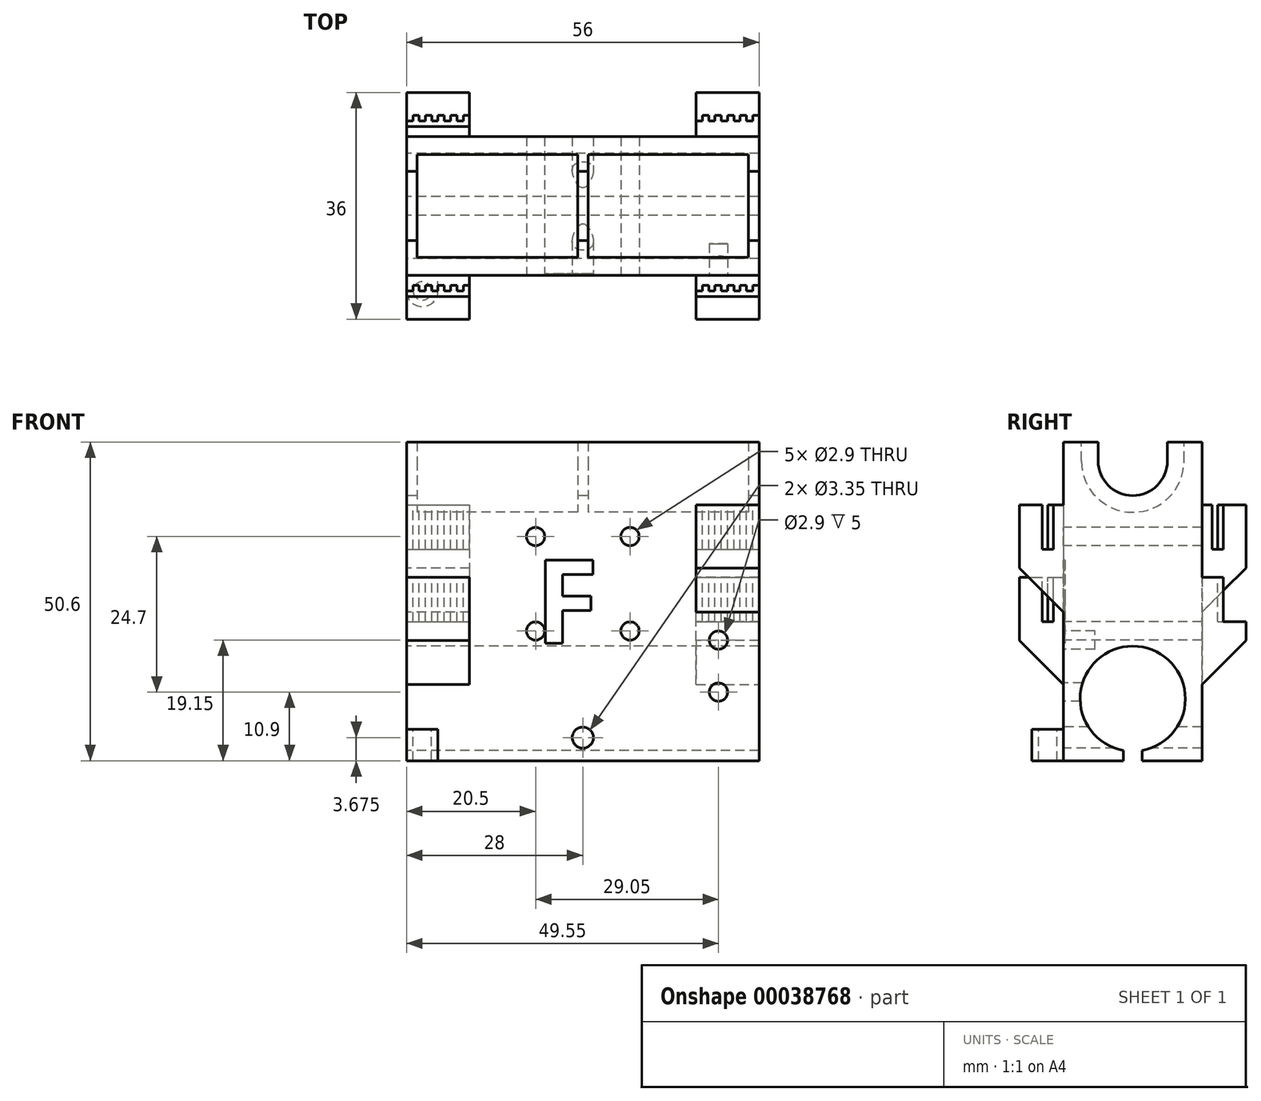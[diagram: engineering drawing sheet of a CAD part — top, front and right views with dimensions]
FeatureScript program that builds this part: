
annotation { "Feature Type Name" : "Feature", "Feature Type Description" : "" }
export const myFeature = defineFeature(function(context is Context, id is Id, definition is map)
    precondition{}
    {
        {
            assignVariable(context, id + "F0", {"name" : "LM8LUU", "anyValue" : 25.5});
        }
        {
            assignVariable(context, id + "F1", {"name" : "length", "anyValue" : 56});
        }
        {
            assignVariable(context, id + "F2", {"name" : "height", "anyValue" : 50.6});
        }
        {
            assignVariable(context, id + "F3", {"name" : "divider", "anyValue" : (getVariable(context, 'length') - 2 * getVariable(context, 'LM8LUU')) / 3});
        }
        {
            var Q0;
            Q0=qCreatedBy(makeId("Top.planeOp"),FACE);
            var sketch = newSketch(context, id + "F4", { "sketchPlane" : qUnion([Q0])});
            skLineSegment(sketch, "E0.bottom", {"start": v(0, 0) * mm, "end": v(56, 0) * mm});
            skLineSegment(sketch, "E0.top", {"start": v(0, 22) * mm, "end": v(56, 22) * mm});
            skLineSegment(sketch, "E0.left", {"start": v(0, 0) * mm, "end": v(0, 22) * mm});
            skLineSegment(sketch, "E0.right", {"start": v(56, 0) * mm, "end": v(56, 22) * mm});
            skSolve(sketch);
        }
        {
            var Q0;
            Q0=qSketchRegion(id+"F4",true);
            extrude(context, id + "F5", {"entities" : qUnion([Q0]), "depth" : (getVariable(context, 'height')) * mm});
        }
        {
            var Q0;
            Q0=makeQuery(id+"F5.opExtrude","SWEPT_FACE",FACE,{"disambiguationData":[OSD([sQuery(id+"F4.wireOp",EDGE,"E0.left")])]});
            var sketch = newSketch(context, id + "F6", { "sketchPlane" : qUnion([Q0])});
            skCircle(sketch, "E1", {"center": v(-11, 9.85) * mm, "radius": 8.35 * mm});
            skCircle(sketch, "E2", {"center": v(-11, 47.6) * mm, "radius": 5.5 * mm});
            skLineSegment(sketch, "E3", {"start": v(-22, 47.6) * mm, "end": v(0, 47.6) * mm, "construction": true});
            skLineSegment(sketch, "E4", {"start": v(-16.5, 50.6) * mm, "end": v(-16.5, 47.6) * mm});
            skLineSegment(sketch, "E5", {"start": v(-5.5, 50.6) * mm, "end": v(-5.5, 47.6) * mm});
            skLineSegment(sketch, "E6", {"start": v(-22, 9.85) * mm, "end": v(0, 9.85) * mm, "construction": true});
            skLineSegment(sketch, "E7", {"start": v(-11, 9.85) * mm, "end": v(-11, 0) * mm, "construction": true});
            skLineSegment(sketch, "E8", {"start": v(-11, 0) * mm, "end": v(-12.5, 0) * mm});
            skLineSegment(sketch, "E9", {"start": v(-12.5, 0) * mm, "end": v(-12.5, 1.64) * mm});
            skLineSegment(sketch, "E10", {"start": v(-12.5, 1.64) * mm, "end": v(-9.5, 1.64) * mm});
            skLineSegment(sketch, "E11", {"start": v(-9.5, 1.64) * mm, "end": v(-9.5, 0) * mm});
            skLineSegment(sketch, "E12", {"start": v(-9.5, 0) * mm, "end": v(-11, 0) * mm});
            skLineSegment(sketch, "E13", {"start": v(-11, 15.6) * mm, "end": v(-11, 18.2) * mm});
            skLineSegment(sketch, "E14", {"start": v(-11, 15.6) * mm, "end": v(-6.05, 16.58) * mm});
            skLineSegment(sketch, "E15", {"start": v(-11, 15.6) * mm, "end": v(-15.95, 16.58) * mm});
            skCircle(sketch, "E16", {"center": v(-11, 47.6) * mm, "radius": 8.15 * mm});
            skLineSegment(sketch, "E17", {"start": v(-2.85, 47.6) * mm, "end": v(-2.85, 50.6) * mm});
            skLineSegment(sketch, "E18", {"start": v(-19.15, 47.6) * mm, "end": v(-19.15, 50.6) * mm});
            skSolve(sketch);
        }
        {
            var Q0;
            {var subQ0=sQuery(id+"F6.wireOp",EDGE,"E14");var subQ1=sQuery(id+"F6.wireOp",EDGE,"E1");var subQ3=makeQuery(id+"F6.imprint","INTERSECT",VERTEX,{"disambiguationData":[OD(0.0)],"derivedFrom":[subQ1,subQ0]});Q0=makeQuery(id+"F6.imprint","IMPRINT",FACE,{"disambiguationData":[TD([[makeQuery(id+"F6.imprint","IMPRINT",EDGE,{"disambiguationData":[TD([[subQ3,-1.0]])],"derivedFrom":subQ1}),1.0]])]});}
            var Q1;
            {var subQ0=sQuery(id+"F6.wireOp",EDGE,"E15");var subQ1=sQuery(id+"F6.wireOp",EDGE,"E1");var subQ3=makeQuery(id+"F6.imprint","INTERSECT",VERTEX,{"disambiguationData":[OD(0.0)],"derivedFrom":[subQ1,subQ0]});Q1=makeQuery(id+"F6.imprint","IMPRINT",FACE,{"disambiguationData":[TD([[makeQuery(id+"F6.imprint","IMPRINT",EDGE,{"disambiguationData":[TD([[subQ3,1.0]])],"derivedFrom":subQ1}),1.0]])]});}
            var Q2;
            Q2=makeQuery(id+"F6.imprint","IMPRINT",FACE,{"disambiguationData":[TD([[makeQuery(id+"F6.imprint","IMPRINT",EDGE,{"derivedFrom":sQuery(id+"F6.wireOp",EDGE,"E8")}),-1.0]])]});
            var Q3;
            {var subQ0=sQuery(id+"F6.wireOp",EDGE,"E10");Q3=makeQuery(id+"F6.imprint","IMPRINT",FACE,{"disambiguationData":[TD([[makeQuery(id+"F6.imprint","IMPRINT",EDGE,{"derivedFrom":subQ0}),-1.0]])]});}
            var Q4;
            {var subQ3=sQuery(id+"F6.wireOp",EDGE,"E13");Q4=makeQuery(id+"F6.imprint","IMPRINT",FACE,{"disambiguationData":[TD([[makeQuery(id+"F6.imprint","IMPRINT",EDGE,{"derivedFrom":subQ3}),-1.0]])]});}
            var Q5;
            {var subQ3=sQuery(id+"F6.wireOp",EDGE,"E13");Q5=makeQuery(id+"F6.imprint","IMPRINT",FACE,{"disambiguationData":[TD([[makeQuery(id+"F6.imprint","IMPRINT",EDGE,{"derivedFrom":subQ3}),1.0]])]});}
            var Q6;
            {var subQ7=sQuery(id+"F6.wireOp",EDGE,"E10");Q6=makeQuery(id+"F6.imprint","IMPRINT",FACE,{"disambiguationData":[TD([[makeQuery(id+"F6.imprint","IMPRINT",EDGE,{"derivedFrom":subQ7}),1.0]])]});}
            var Q7;
            {var subQ3=sQuery(id+"F6.wireOp",EDGE,"E5");Q7=makeQuery(id+"F6.imprint","IMPRINT",FACE,{"disambiguationData":[TD([[makeQuery(id+"F6.imprint","IMPRINT",EDGE,{"derivedFrom":subQ3}),-1.0]])]});}
            var Q8;
            {var subQ0=sQuery(id+"F6.wireOp",EDGE,"E4");Q8=makeQuery(id+"F6.imprint","IMPRINT",FACE,{"disambiguationData":[TD([[makeQuery(id+"F6.imprint","IMPRINT",EDGE,{"derivedFrom":subQ0}),1.0]])]});}
            var Q9;
            {var subQ0=sQuery(id+"F6.wireOp",EDGE,"E4");Q9=makeQuery(id+"F6.imprint","IMPRINT",FACE,{"disambiguationData":[TD([[makeQuery(id+"F6.imprint","IMPRINT",EDGE,{"derivedFrom":subQ0}),1.0]])]});}
            var Q10;
            {var subQ3=sQuery(id+"F6.wireOp",EDGE,"E5");Q10=makeQuery(id+"F6.imprint","IMPRINT",FACE,{"disambiguationData":[TD([[makeQuery(id+"F6.imprint","IMPRINT",EDGE,{"derivedFrom":subQ3}),-1.0]])]});}
            var Q11;
            {var subQ1=sQuery(id+"F6.wireOp",EDGE,"E2");var subQ4=makeQuery(id+"F6.imprint","INTERSECT",VERTEX,{"derivedFrom":[subQ1,sQuery(id+"F6.wireOp",EDGE,"E5")]});Q11=makeQuery(id+"F6.imprint","IMPRINT",FACE,{"disambiguationData":[TD([[makeQuery(id+"F6.imprint","IMPRINT",EDGE,{"disambiguationData":[TD([[subQ4,-1.0]])],"derivedFrom":subQ1}),1.0]])]});}
            extrude(context, id + "F7", {"entities" : qUnion([Q0, Q1, Q2, Q3, Q4, Q5, Q6, Q7, Q8, Q9, Q10, Q11]), "operationType" : NewBodyOperationType.REMOVE, "endBound" : BoundingType.THROUGH_ALL, "oppositeDirection" : true, "depth" : 25 * mm});
        }
        {
            var Q0;
            {var subQ6=sQuery(id+"F6.wireOp",EDGE,"E4");Q0=makeQuery(id+"F6.imprint","IMPRINT",FACE,{"disambiguationData":[TD([[makeQuery(id+"F6.imprint","IMPRINT",EDGE,{"derivedFrom":subQ6}),-1.0]])]});}
            var Q1;
            {var subQ0=sQuery(id+"F6.wireOp",EDGE,"E18");Q1=makeQuery(id+"F6.imprint","IMPRINT",FACE,{"disambiguationData":[TD([[makeQuery(id+"F6.imprint","IMPRINT",EDGE,{"derivedFrom":subQ0}),-1.0]])]});}
            var Q2;
            {var subQ0=sQuery(id+"F6.wireOp",EDGE,"E17");Q2=makeQuery(id+"F6.imprint","IMPRINT",FACE,{"disambiguationData":[TD([[makeQuery(id+"F6.imprint","IMPRINT",EDGE,{"derivedFrom":subQ0}),1.0]])]});}
            extrude(context, id + "F8", {"entities" : qUnion([Q0, Q1, Q2]), "operationType" : NewBodyOperationType.REMOVE, "oppositeDirection" : true, "depth" : (getVariable(context, 'divider') + (getVariable(context, 'LM8LUU'))) * mm, "hasSecondDirection" : true, "secondDirectionOppositeDirection" : true, "secondDirectionDepth" : (getVariable(context, 'divider')) * mm});
        }
        {
            var Q0;
            Q0=makeQuery(id+"F8.boolean.opBoolean","COPY",FACE,{"derivedFrom":makeQuery(id+"F8.opExtrude","CAP_FACE",FACE,{"disambiguationData":[OSD([sQuery(id+"F4.wireOp",EDGE,"E0.left"),sQuery(id+"F6.wireOp",EDGE,"E2"),sQuery(id+"F6.wireOp",EDGE,"E4"),sQuery(id+"F6.wireOp",EDGE,"E5"),sQuery(id+"F6.wireOp",EDGE,"E16"),sQuery(id+"F6.wireOp",EDGE,"E17"),sQuery(id+"F6.wireOp",EDGE,"E18")])],"isStart":false})});
            extrude(context, id + "F9", {"entities" : qUnion([Q0]), "operationType" : NewBodyOperationType.REMOVE, "oppositeDirection" : true, "depth" : (getVariable(context, 'divider') + getVariable(context, 'LM8LUU')) * mm, "hasSecondDirection" : true, "secondDirectionOppositeDirection" : true, "secondDirectionDepth" : (getVariable(context, 'divider')) * mm});
        }
        {
            var Q0;
            Q0=makeQuery(id+"F5.opExtrude","SWEPT_FACE",FACE,{"disambiguationData":[OSD([sQuery(id+"F4.wireOp",EDGE,"E0.bottom")])]});
            var sketch = newSketch(context, id + "F10", { "sketchPlane" : qUnion([Q0])});
            skLineSegment(sketch, "E19.bottom", {"start": v(0, 29.1) * mm, "end": v(10, 29.1) * mm});
            skLineSegment(sketch, "E19.top", {"start": v(0, 9.1) * mm, "end": v(10, 9.1) * mm});
            skLineSegment(sketch, "E19.left", {"start": v(0, 29.1) * mm, "end": v(0, 9.1) * mm});
            skLineSegment(sketch, "E19.right", {"start": v(10, 29.1) * mm, "end": v(10, 9.1) * mm});
            skLineSegment(sketch, "E20.bottom", {"start": v(56, 40.6) * mm, "end": v(46, 40.6) * mm});
            skLineSegment(sketch, "E20.top", {"start": v(56, 20.6) * mm, "end": v(46, 20.6) * mm});
            skLineSegment(sketch, "E20.left", {"start": v(56, 40.6) * mm, "end": v(56, 20.6) * mm});
            skLineSegment(sketch, "E20.right", {"start": v(46, 40.6) * mm, "end": v(46, 20.6) * mm});
            skPoint(sketch, "E21", {"position": v(0, 47.6) * mm});
            skPoint(sketch, "E22", {"position": v(0, 8.6) * mm});
            skSolve(sketch);
        }
        {
            var Q0;
            Q0=qSketchRegion(id+"F10",true);
            extrude(context, id + "F11", {"entities" : qUnion([Q0]), "operationType" : NewBodyOperationType.ADD, "depth" : 7 * mm});
        }
        {
            var Q0;
            Q0=makeQuery(id+"F11.opExtrude","CAP_EDGE",EDGE,{"disambiguationData":[OSD([sQuery(id+"F10.wireOp",EDGE,"E19.top")])],"isStart":false});
            var Q1;
            Q1=makeQuery(id+"F11.opExtrude","CAP_EDGE",EDGE,{"disambiguationData":[OSD([sQuery(id+"F10.wireOp",EDGE,"E20.top")])],"isStart":false});
            chamfer(context, id + "F12", {"entities" : qUnion([Q0, Q1]), "width" : 10 * mm, "tangentPropagation" : true});
        }
        {
            var Q0;
            Q0=makeQuery(id+"F11.opExtrude","SWEPT_FACE",FACE,{"disambiguationData":[OSD([sQuery(id+"F10.wireOp",EDGE,"E19.bottom")])]});
            var sketch = newSketch(context, id + "F13", { "sketchPlane" : qUnion([Q0])});
            skLineSegment(sketch, "E23", {"start": v(-935.9, 0) * mm, "end": v(-935.88, -4.54) * mm});
            skLineSegment(sketch, "E24.left", {"start": v(0, -3.4) * mm, "end": v(0, -1.6) * mm});
            skLineSegment(sketch, "E25", {"start": v(6, -2.5) * mm, "end": v(7, -2.5) * mm});
            skLineSegment(sketch, "E26", {"start": v(4, -2.5) * mm, "end": v(5, -2.5) * mm});
            skLineSegment(sketch, "E27", {"start": v(0, -2.5) * mm, "end": v(1, -2.5) * mm});
            skLineSegment(sketch, "E28", {"start": v(7, -1.6) * mm, "end": v(8, -1.6) * mm});
            skLineSegment(sketch, "E29", {"start": v(2, -2.5) * mm, "end": v(3, -2.5) * mm});
            skLineSegment(sketch, "E30", {"start": v(3, -1.6) * mm, "end": v(4, -1.6) * mm});
            skLineSegment(sketch, "E31", {"start": v(8, -2.5) * mm, "end": v(9, -2.5) * mm});
            skLineSegment(sketch, "E32", {"start": v(8, -1.6) * mm, "end": v(8, -2.5) * mm});
            skLineSegment(sketch, "E33", {"start": v(9, -2.5) * mm, "end": v(9, -1.6) * mm});
            skLineSegment(sketch, "E34", {"start": v(10, -1.6) * mm, "end": v(10, -2.5) * mm});
            skLineSegment(sketch, "E35", {"start": v(6, -1.6) * mm, "end": v(6, -2.5) * mm});
            skLineSegment(sketch, "E36", {"start": v(2, -1.6) * mm, "end": v(2, -2.5) * mm});
            skLineSegment(sketch, "E37", {"start": v(1, -1.6) * mm, "end": v(2, -1.6) * mm});
            skLineSegment(sketch, "E38", {"start": v(1, -2.5) * mm, "end": v(1, -1.6) * mm});
            skLineSegment(sketch, "E39", {"start": v(9, -1.6) * mm, "end": v(10, -1.6) * mm});
            skLineSegment(sketch, "E40", {"start": v(5, -1.6) * mm, "end": v(6, -1.6) * mm});
            skLineSegment(sketch, "E41", {"start": v(5, -2.5) * mm, "end": v(5, -1.6) * mm});
            skLineSegment(sketch, "E42", {"start": v(3, -2.5) * mm, "end": v(3, -1.6) * mm});
            skLineSegment(sketch, "E43", {"start": v(4, -1.6) * mm, "end": v(4, -2.5) * mm});
            skLineSegment(sketch, "E44", {"start": v(7, -2.5) * mm, "end": v(7, -1.6) * mm});
            skLineSegment(sketch, "E45", {"start": v(0, -1.6) * mm, "end": v(0, -2.5) * mm});
            skLineSegment(sketch, "E46", {"start": v(10, -2.5) * mm, "end": v(10, -3.4) * mm});
            skLineSegment(sketch, "E47", {"start": v(0, -3.4) * mm, "end": v(10, -3.4) * mm});
            skLineSegment(sketch, "E48", {"start": v(5.3, -1.6) * mm, "end": v(5.3, 0) * mm});
            skSolve(sketch);
        }
        {
            var Q0;
            Q0=qSketchRegion(id+"F13",true);
            extrude(context, id + "F14", {"entities" : qUnion([Q0]), "operationType" : NewBodyOperationType.REMOVE, "oppositeDirection" : true, "depth" : 7 * mm});
        }
        {
            var Q0;
            Q0=makeQuery(id+"F11.opExtrude","SWEPT_FACE",FACE,{"disambiguationData":[OSD([sQuery(id+"F10.wireOp",EDGE,"E20.bottom")])]});
            var sketch = newSketch(context, id + "F15", { "sketchPlane" : qUnion([Q0])});
            skLineSegment(sketch, "E49.left", {"start": v(46, -3.4) * mm, "end": v(46, -1.6) * mm});
            skLineSegment(sketch, "E50", {"start": v(52, -2.5) * mm, "end": v(53, -2.5) * mm});
            skLineSegment(sketch, "E51", {"start": v(50, -2.5) * mm, "end": v(51, -2.5) * mm});
            skLineSegment(sketch, "E52", {"start": v(46, -2.5) * mm, "end": v(47, -2.5) * mm});
            skLineSegment(sketch, "E53", {"start": v(53, -1.6) * mm, "end": v(54, -1.6) * mm});
            skLineSegment(sketch, "E54", {"start": v(48, -2.5) * mm, "end": v(49, -2.5) * mm});
            skLineSegment(sketch, "E55", {"start": v(49, -1.6) * mm, "end": v(50, -1.6) * mm});
            skLineSegment(sketch, "E56", {"start": v(54, -2.5) * mm, "end": v(55, -2.5) * mm});
            skLineSegment(sketch, "E57", {"start": v(54, -1.6) * mm, "end": v(54, -2.5) * mm});
            skLineSegment(sketch, "E58", {"start": v(55, -2.5) * mm, "end": v(55, -1.6) * mm});
            skLineSegment(sketch, "E59", {"start": v(56, -1.6) * mm, "end": v(56, -2.5) * mm});
            skLineSegment(sketch, "E60", {"start": v(52, -1.6) * mm, "end": v(52, -2.5) * mm});
            skLineSegment(sketch, "E61", {"start": v(48, -1.6) * mm, "end": v(48, -2.5) * mm});
            skLineSegment(sketch, "E62", {"start": v(47, -1.6) * mm, "end": v(48, -1.6) * mm});
            skLineSegment(sketch, "E63", {"start": v(47, -2.5) * mm, "end": v(47, -1.6) * mm});
            skLineSegment(sketch, "E64", {"start": v(55, -1.6) * mm, "end": v(56, -1.6) * mm});
            skLineSegment(sketch, "E65", {"start": v(51, -1.6) * mm, "end": v(52, -1.6) * mm});
            skLineSegment(sketch, "E66", {"start": v(51, -2.5) * mm, "end": v(51, -1.6) * mm});
            skLineSegment(sketch, "E67", {"start": v(49, -2.5) * mm, "end": v(49, -1.6) * mm});
            skLineSegment(sketch, "E68", {"start": v(50, -1.6) * mm, "end": v(50, -2.5) * mm});
            skLineSegment(sketch, "E69", {"start": v(53, -2.5) * mm, "end": v(53, -1.6) * mm});
            skLineSegment(sketch, "E70", {"start": v(46, -1.6) * mm, "end": v(46, -2.5) * mm});
            skLineSegment(sketch, "E71", {"start": v(56, -2.5) * mm, "end": v(56, -3.4) * mm});
            skLineSegment(sketch, "E72", {"start": v(46, -3.4) * mm, "end": v(56, -3.4) * mm});
            skLineSegment(sketch, "E73", {"start": v(51.23, -1.6) * mm, "end": v(51.23, 0) * mm});
            skSolve(sketch);
        }
        {
            var Q0;
            Q0=qSketchRegion(id+"F15",true);
            extrude(context, id + "F16", {"entities" : qUnion([Q0]), "operationType" : NewBodyOperationType.REMOVE, "oppositeDirection" : true, "depth" : 7 * mm});
        }
        {
            var Q0;
            Q0=makeQuery(id+"F5.opExtrude","SWEPT_FACE",FACE,{"disambiguationData":[OSD([sQuery(id+"F4.wireOp",EDGE,"E0.top")])]});
            var sketch = newSketch(context, id + "F17", { "sketchPlane" : qUnion([Q0])});
            skLineSegment(sketch, "E74.bottom", {"start": v(-56, 9.1) * mm, "end": v(-46, 9.1) * mm});
            skLineSegment(sketch, "E74.top", {"start": v(-56, 29.1) * mm, "end": v(-46, 29.1) * mm});
            skLineSegment(sketch, "E74.left", {"start": v(-56, 9.1) * mm, "end": v(-56, 29.1) * mm});
            skLineSegment(sketch, "E74.right", {"start": v(-46, 9.1) * mm, "end": v(-46, 29.1) * mm});
            skLineSegment(sketch, "E75.bottom", {"start": v(0, 40.6) * mm, "end": v(-10, 40.6) * mm});
            skLineSegment(sketch, "E75.top", {"start": v(0, 20.6) * mm, "end": v(-10, 20.6) * mm});
            skLineSegment(sketch, "E75.left", {"start": v(0, 40.6) * mm, "end": v(0, 20.6) * mm});
            skLineSegment(sketch, "E75.right", {"start": v(-10, 40.6) * mm, "end": v(-10, 20.6) * mm});
            skSolve(sketch);
        }
        {
            var Q0;
            Q0=qSketchRegion(id+"F17",true);
            extrude(context, id + "F18", {"entities" : qUnion([Q0]), "operationType" : NewBodyOperationType.ADD, "depth" : 7 * mm});
        }
        {
            var Q0;
            Q0=makeQuery(id+"F18.opExtrude","SWEPT_FACE",FACE,{"disambiguationData":[OSD([sQuery(id+"F17.wireOp",EDGE,"E74.top")])]});
            var sketch = newSketch(context, id + "F19", { "sketchPlane" : qUnion([Q0])});
            skLineSegment(sketch, "E76.left", {"start": v(46, 23.6) * mm, "end": v(46, 25.4) * mm});
            skLineSegment(sketch, "E77", {"start": v(52, 24.5) * mm, "end": v(53, 24.5) * mm});
            skLineSegment(sketch, "E78", {"start": v(50, 24.5) * mm, "end": v(51, 24.5) * mm});
            skLineSegment(sketch, "E79", {"start": v(46, 24.5) * mm, "end": v(47, 24.5) * mm});
            skLineSegment(sketch, "E80", {"start": v(53, 25.4) * mm, "end": v(54, 25.4) * mm});
            skLineSegment(sketch, "E81", {"start": v(48, 24.5) * mm, "end": v(49, 24.5) * mm});
            skLineSegment(sketch, "E82", {"start": v(49, 25.4) * mm, "end": v(50, 25.4) * mm});
            skLineSegment(sketch, "E83", {"start": v(54, 24.5) * mm, "end": v(55, 24.5) * mm});
            skLineSegment(sketch, "E84", {"start": v(54, 25.4) * mm, "end": v(54, 24.5) * mm});
            skLineSegment(sketch, "E85", {"start": v(55, 24.5) * mm, "end": v(55, 25.4) * mm});
            skLineSegment(sketch, "E86", {"start": v(56, 25.4) * mm, "end": v(56, 24.5) * mm});
            skLineSegment(sketch, "E87", {"start": v(52, 25.4) * mm, "end": v(52, 24.5) * mm});
            skLineSegment(sketch, "E88", {"start": v(48, 25.4) * mm, "end": v(48, 24.5) * mm});
            skLineSegment(sketch, "E89", {"start": v(47, 25.4) * mm, "end": v(48, 25.4) * mm});
            skLineSegment(sketch, "E90", {"start": v(47, 24.5) * mm, "end": v(47, 25.4) * mm});
            skLineSegment(sketch, "E91", {"start": v(55, 25.4) * mm, "end": v(56, 25.4) * mm});
            skLineSegment(sketch, "E92", {"start": v(51, 25.4) * mm, "end": v(52, 25.4) * mm});
            skLineSegment(sketch, "E93", {"start": v(51, 24.5) * mm, "end": v(51, 25.4) * mm});
            skLineSegment(sketch, "E94", {"start": v(49, 24.5) * mm, "end": v(49, 25.4) * mm});
            skLineSegment(sketch, "E95", {"start": v(50, 25.4) * mm, "end": v(50, 24.5) * mm});
            skLineSegment(sketch, "E96", {"start": v(53, 24.5) * mm, "end": v(53, 25.4) * mm});
            skLineSegment(sketch, "E97", {"start": v(46, 25.4) * mm, "end": v(46, 24.5) * mm});
            skLineSegment(sketch, "E98", {"start": v(56, 24.5) * mm, "end": v(56, 23.6) * mm});
            skLineSegment(sketch, "E99", {"start": v(46, 23.6) * mm, "end": v(56, 23.6) * mm});
            skLineSegment(sketch, "E100", {"start": v(51, 23.6) * mm, "end": v(51, 22) * mm});
            skSolve(sketch);
        }
        {
            var Q0;
            {var subQ4=sQuery(id+"F19.wireOp",EDGE,"E76.left");Q0=makeQuery(id+"F19.imprint","IMPRINT",FACE,{"disambiguationData":[TD([[makeQuery(id+"F19.imprint","IMPRINT",EDGE,{"derivedFrom":subQ4}),1.0]])]});}
            extrude(context, id + "F20", {"entities" : qUnion([Q0]), "operationType" : NewBodyOperationType.REMOVE, "oppositeDirection" : true, "depth" : 7 * mm});
        }
        {
            var Q0;
            Q0=makeQuery(id+"F18.opExtrude","SWEPT_FACE",FACE,{"disambiguationData":[OSD([sQuery(id+"F17.wireOp",EDGE,"E75.bottom")])]});
            var sketch = newSketch(context, id + "F21", { "sketchPlane" : qUnion([Q0])});
            skLineSegment(sketch, "E101", {"start": v(6, 24.5) * mm, "end": v(7, 24.5) * mm});
            skLineSegment(sketch, "E102", {"start": v(4, 24.5) * mm, "end": v(5, 24.5) * mm});
            skLineSegment(sketch, "E103", {"start": v(0, 24.5) * mm, "end": v(1, 24.5) * mm});
            skLineSegment(sketch, "E104", {"start": v(7, 25.4) * mm, "end": v(8, 25.4) * mm});
            skLineSegment(sketch, "E105", {"start": v(2, 24.5) * mm, "end": v(3, 24.5) * mm});
            skLineSegment(sketch, "E106", {"start": v(3, 25.4) * mm, "end": v(4, 25.4) * mm});
            skLineSegment(sketch, "E107", {"start": v(8, 24.5) * mm, "end": v(9, 24.5) * mm});
            skLineSegment(sketch, "E108", {"start": v(8, 25.4) * mm, "end": v(8, 24.5) * mm});
            skLineSegment(sketch, "E109", {"start": v(9, 24.5) * mm, "end": v(9, 25.4) * mm});
            skLineSegment(sketch, "E110", {"start": v(10, 25.4) * mm, "end": v(10, 24.5) * mm});
            skLineSegment(sketch, "E111", {"start": v(6, 25.4) * mm, "end": v(6, 24.5) * mm});
            skLineSegment(sketch, "E112", {"start": v(2, 25.4) * mm, "end": v(2, 24.5) * mm});
            skLineSegment(sketch, "E113", {"start": v(1, 25.4) * mm, "end": v(2, 25.4) * mm});
            skLineSegment(sketch, "E114", {"start": v(1, 24.5) * mm, "end": v(1, 25.4) * mm});
            skLineSegment(sketch, "E115", {"start": v(9, 25.4) * mm, "end": v(10, 25.4) * mm});
            skLineSegment(sketch, "E116", {"start": v(5, 25.4) * mm, "end": v(6, 25.4) * mm});
            skLineSegment(sketch, "E117", {"start": v(5, 24.5) * mm, "end": v(5, 25.4) * mm});
            skLineSegment(sketch, "E118", {"start": v(3, 24.5) * mm, "end": v(3, 25.4) * mm});
            skLineSegment(sketch, "E119", {"start": v(4, 25.4) * mm, "end": v(4, 24.5) * mm});
            skLineSegment(sketch, "E120", {"start": v(7, 24.5) * mm, "end": v(7, 25.4) * mm});
            skLineSegment(sketch, "E121", {"start": v(10, 24.5) * mm, "end": v(10, 23.6) * mm});
            skLineSegment(sketch, "E122", {"start": v(0, 23.6) * mm, "end": v(10, 23.6) * mm});
            skLineSegment(sketch, "E123", {"start": v(5, 23.6) * mm, "end": v(5, 22) * mm});
            skLineSegment(sketch, "E124", {"start": v(0, 23.6) * mm, "end": v(0, 24.5) * mm});
            skSolve(sketch);
        }
        {
            var Q0;
            Q0=makeQuery(id+"F21.imprint","IMPRINT",FACE,{"disambiguationData":[TD([[makeQuery(id+"F21.imprint","IMPRINT",EDGE,{"derivedFrom":sQuery(id+"F21.wireOp",EDGE,"E101")}),-1.0]])]});
            extrude(context, id + "F22", {"entities" : qUnion([Q0]), "operationType" : NewBodyOperationType.REMOVE, "oppositeDirection" : true, "depth" : 7 * mm});
        }
        {
            var Q0;
            Q0=makeQuery(id+"F18.opExtrude","CAP_EDGE",EDGE,{"disambiguationData":[OSD([sQuery(id+"F17.wireOp",EDGE,"E75.top")])],"isStart":false});
            var Q1;
            Q1=makeQuery(id+"F18.opExtrude","CAP_EDGE",EDGE,{"disambiguationData":[OSD([sQuery(id+"F17.wireOp",EDGE,"E74.bottom")])],"isStart":false});
            chamfer(context, id + "F23", {"entities" : qUnion([Q0, Q1]), "width" : 10 * mm, "tangentPropagation" : true});
        }
        {
            var Q0;
            Q0=makeQuery(id+"F5.opExtrude","SWEPT_FACE",FACE,{"disambiguationData":[OSD([sQuery(id+"F4.wireOp",EDGE,"E0.bottom")])]});
            var sketch = newSketch(context, id + "F24", { "sketchPlane" : qUnion([Q0])});
            skCircle(sketch, "E125", {"center": v(20.5, 35.6) * mm, "radius": 1.45 * mm});
            skCircle(sketch, "E126", {"center": v(35.5, 35.6) * mm, "radius": 1.45 * mm});
            skCircle(sketch, "E127", {"center": v(20.5, 20.6) * mm, "radius": 1.45 * mm});
            skCircle(sketch, "E128", {"center": v(35.5, 20.6) * mm, "radius": 1.45 * mm});
            skLineSegment(sketch, "E129", {"start": v(20.5, 35.6) * mm, "end": v(0, 35.6) * mm});
            skLineSegment(sketch, "E130", {"start": v(35.5, 20.6) * mm, "end": v(56, 20.6) * mm});
            skLineSegment(sketch, "E131", {"start": v(35.5, 35.6) * mm, "end": v(35.5, 50.6) * mm});
            skLineSegment(sketch, "E132", {"start": v(20.5, 20.6) * mm, "end": v(20.5, 0) * mm});
            skCircle(sketch, "E133", {"center": v(28, 3.68) * mm, "radius": 1.68 * mm});
            skLineSegment(sketch, "E134", {"start": v(28, 0) * mm, "end": v(28, 13.82) * mm, "construction": true});
            skSolve(sketch);
        }
        {
            var Q0;
            Q0=qSketchRegion(id+"F24",true);
            var Q1;
            Q1=makeQuery(id+"F24.imprint","IMPRINT",FACE,{"disambiguationData":[TD([[makeQuery(id+"F24.imprint","IMPRINT",EDGE,{"derivedFrom":sQuery(id+"F24.wireOp",EDGE,"E125")}),1.0]])]});
            var Q2;
            Q2=makeQuery(id+"F24.imprint","IMPRINT",FACE,{"disambiguationData":[TD([[makeQuery(id+"F24.imprint","IMPRINT",EDGE,{"derivedFrom":sQuery(id+"F24.wireOp",EDGE,"E126")}),1.0]])]});
            var Q3;
            Q3=makeQuery(id+"F24.imprint","IMPRINT",FACE,{"disambiguationData":[TD([[makeQuery(id+"F24.imprint","IMPRINT",EDGE,{"derivedFrom":sQuery(id+"F24.wireOp",EDGE,"E128")}),1.0]])]});
            var Q4;
            Q4=makeQuery(id+"F24.imprint","IMPRINT",FACE,{"disambiguationData":[TD([[makeQuery(id+"F24.imprint","IMPRINT",EDGE,{"derivedFrom":sQuery(id+"F24.wireOp",EDGE,"E127")}),1.0]])]});
            extrude(context, id + "F25", {"entities" : qUnion([Q0, Q1, Q2, Q3, Q4]), "operationType" : NewBodyOperationType.REMOVE, "endBound" : BoundingType.THROUGH_ALL, "oppositeDirection" : true, "depth" : 25 * mm});
        }
        {
            var Q0;
            Q0=makeQuery(id+"F5.opExtrude","SWEPT_FACE",FACE,{"disambiguationData":[OSD([sQuery(id+"F4.wireOp",EDGE,"E0.bottom")])]});
            var sketch = newSketch(context, id + "F26", { "sketchPlane" : qUnion([Q0])});
            skCircle(sketch, "E135", {"center": v(49.55, 19.15) * mm, "radius": 1.45 * mm});
            skCircle(sketch, "E136", {"center": v(49.55, 10.9) * mm, "radius": 1.45 * mm});
            skSolve(sketch);
        }
        {
            var Q0;
            Q0=qSketchRegion(id+"F26",true);
            extrude(context, id + "F27", {"entities" : qUnion([Q0]), "operationType" : NewBodyOperationType.REMOVE, "oppositeDirection" : true, "depth" : 5 * mm});
        }
        {
            var Q0;
            Q0=makeQuery(id+"F5.opExtrude","SWEPT_FACE",FACE,{"disambiguationData":[OSD([sQuery(id+"F4.wireOp",EDGE,"E0.bottom")])]});
            var sketch = newSketch(context, id + "F28", { "sketchPlane" : qUnion([Q0])});
            skText(sketch, "E137", { "text": "F", "fontName": "OpenSans-Bold.ttf"});
            skLineSegment(sketch, "E138", {"start": v(20.5, 35.6) * mm, "end": v(20.5, 20.6) * mm, "construction": true});
            skLineSegment(sketch, "E139", {"start": v(20.5, 20.6) * mm, "end": v(35.5, 20.6) * mm, "construction": true});
            skLineSegment(sketch, "E140", {"start": v(35.5, 20.6) * mm, "end": v(35.5, 35.6) * mm, "construction": true});
            skLineSegment(sketch, "E141", {"start": v(35.5, 35.6) * mm, "end": v(20.5, 35.6) * mm, "construction": true});
            skLineSegment(sketch, "E142", {"start": v(20.5, 28.1) * mm, "end": v(23.4, 28.1) * mm, "construction": true});
            skLineSegment(sketch, "E143", {"start": v(32.6, 28.1) * mm, "end": v(35.5, 28.1) * mm, "construction": true});
            skLineSegment(sketch, "E144", {"start": v(28, 21.46) * mm, "end": v(28, 20.6) * mm, "construction": true});
            skLineSegment(sketch, "E145", {"start": v(28, 35.6) * mm, "end": v(28, 34.74) * mm, "construction": true});
            const initialGuessF28  = {"E137": [0.0204, 0.01866, 1, 0, 0.01328]};
            skSetInitialGuess(sketch, initialGuessF28);
            skSolve(sketch);
        }
        {
            var Q0;
            Q0=qSketchRegion(id+"F28",true);
            extrude(context, id + "F29", {"entities" : qUnion([Q0]), "operationType" : NewBodyOperationType.REMOVE, "oppositeDirection" : true, "depth" : .25 * mm});
        }
        {
            var Q0;
            Q0=makeQuery(id+"F5.opExtrude","SWEPT_FACE",FACE,{"disambiguationData":[OSD([sQuery(id+"F4.wireOp",EDGE,"E0.bottom")])]});
            var sketch = newSketch(context, id + "F30", { "sketchPlane" : qUnion([Q0])});
            skLineSegment(sketch, "E146.bottom", {"start": v(0, 0) * mm, "end": v(5, 0) * mm});
            skLineSegment(sketch, "E146.top", {"start": v(0, 5) * mm, "end": v(5, 5) * mm});
            skLineSegment(sketch, "E146.left", {"start": v(0, 0) * mm, "end": v(0, 5) * mm});
            skLineSegment(sketch, "E146.right", {"start": v(5, 0) * mm, "end": v(5, 5) * mm});
            skSolve(sketch);
        }
        {
            var Q0;
            Q0=qSketchRegion(id+"F30",true);
            extrude(context, id + "F31", {"entities" : qUnion([Q0]), "operationType" : NewBodyOperationType.ADD, "depth" : 5 * mm});
        }
        {
            var Q0;
            Q0=makeQuery(id+"F31.opExtrude","SWEPT_FACE",FACE,{"disambiguationData":[OSD([sQuery(id+"F30.wireOp",EDGE,"E146.top")])]});
            var sketch = newSketch(context, id + "F32", { "sketchPlane" : qUnion([Q0])});
            skCircle(sketch, "E147", {"center": v(2.5, -2.5) * mm, "radius": 1.45 * mm});
            skLineSegment(sketch, "E148", {"start": v(0, -2.5) * mm, "end": v(5, -2.5) * mm});
            skSolve(sketch);
        }
        {
            var Q0;
            Q0=qSketchRegion(id+"F32",true);
            extrude(context, id + "F33", {"entities" : qUnion([Q0]), "operationType" : NewBodyOperationType.REMOVE, "oppositeDirection" : true, "depth" : 25 * mm});
        }
        {
            var Q0;
            Q0=makeQuery(id+"F31.opExtrude","CAP_EDGE",EDGE,{"disambiguationData":[OSD([sQuery(id+"F30.wireOp",EDGE,"E146.left")])],"isStart":false});
            var Q1;
            Q1=makeQuery(id+"F31.opExtrude","CAP_EDGE",EDGE,{"disambiguationData":[OSD([sQuery(id+"F30.wireOp",EDGE,"E146.right")])],"isStart":false});
            fillet(context, id + "F34", {"entities" : qUnion([Q0, Q1]), "radius" : 2.5 * mm, "tangentPropagation" : true, "allowEdgeOverflow" : false});
        }
    });
